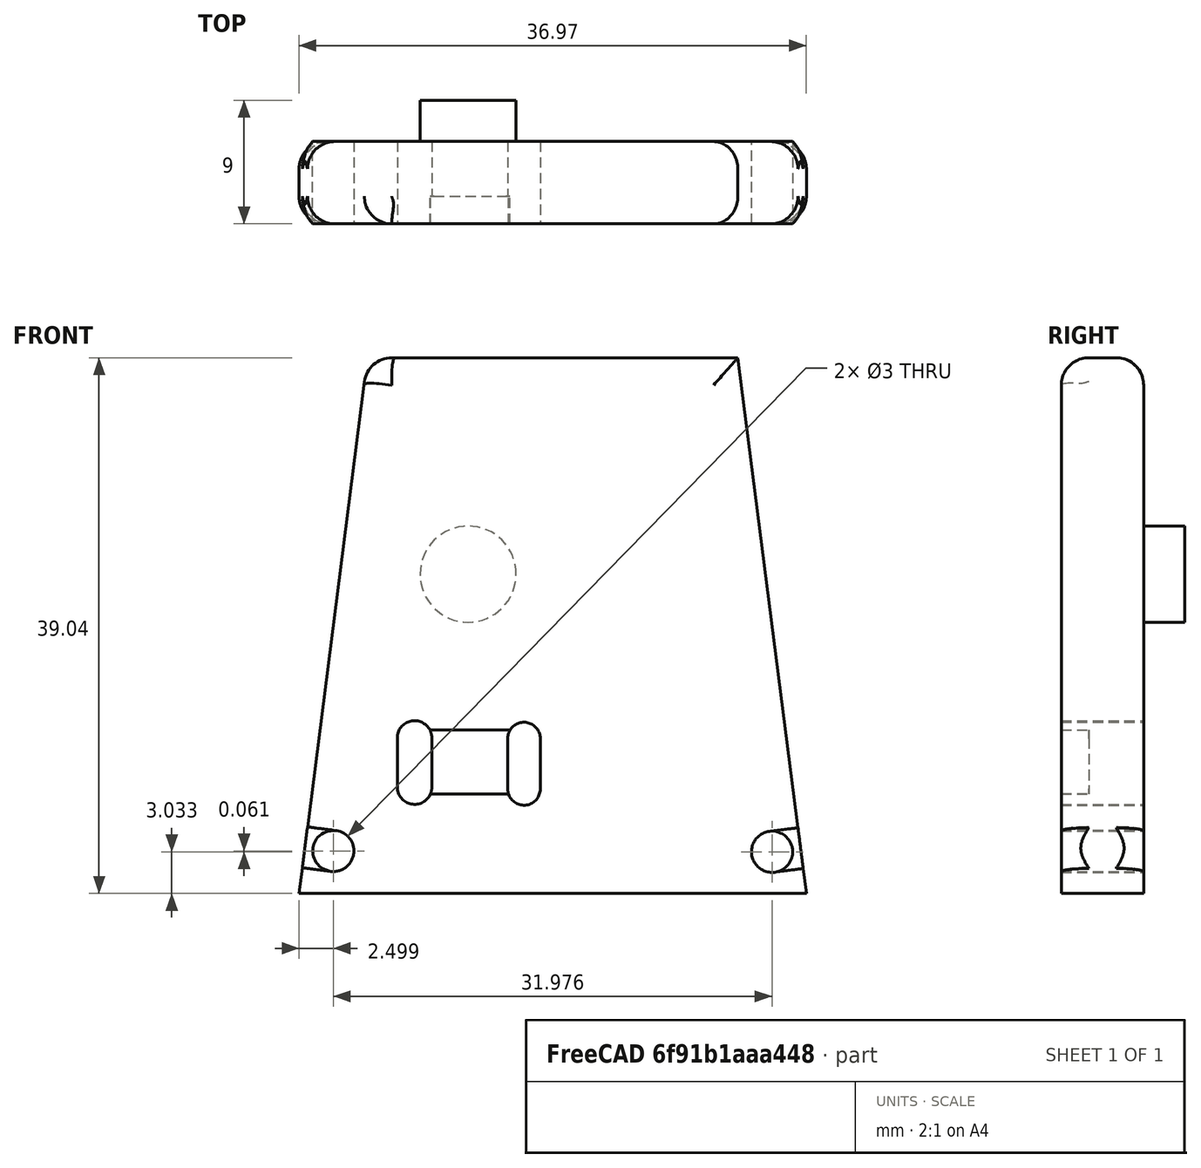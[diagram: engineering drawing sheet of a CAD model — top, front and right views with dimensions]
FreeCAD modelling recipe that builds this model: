
FCSTD DOCUMENT  (FreeCAD 0.17R13519 (Git))
Label: portaGPSinav2
License: All rights reserved
LicenseURL: http://it.wikipedia.org/wiki/<copyright redacted>
objects: Sketcher::SketchObject×5, PartDesign::Pocket×3, PartDesign::Fillet×3, PartDesign::Pad×2, Mesh::Feature×1, PartDesign::Body×1
note: 19 computed .brp shape members not serialized (recipe doc carries the construction recipe); baked Part::Feature solids carry a one-line shape summary decoded from their .brp

FEATURE [Mesh::Feature] ls210_sup
FEATURE [Sketcher::SketchObject] Sketch
  MapMode = 5
  Placement = pos=(0,0,0) rot=(1,0,0;1.5708rad)
  Support = -> [XZ_Plane]
  sketch-geometry (6):
    g0: LineSegment StartX=4.89923 StartY=141.911 StartZ=0 EndX=41.8748 EndY=141.911 EndZ=0
    g1: LineSegment StartX=41.8748 StartY=141.911 StartZ=0 EndX=36.8748 EndY=180.951 EndZ=0
    g2: LineSegment StartX=36.8748 StartY=180.951 StartZ=0 EndX=9.89923 EndY=180.951 EndZ=0
    g3: LineSegment StartX=9.89923 StartY=180.951 StartZ=0 EndX=4.89923 EndY=141.911 EndZ=0
    g4: GeomPoint X=7.39923 Y=144.73 Z=0
    g5: GeomPoint X=39.3748 Y=144.856 Z=0
  constraints (10):
    c: Coincident(g0,g1)
    c: Coincident(g1,g2)
    c: Coincident(g2,g3)
    c: Coincident(g3,g0)
    c: Horizontal(g0)
    c: Horizontal(g2)
    c: DistanceX(g0,g2) = 5
    c: DistanceX(g1,g0) = 5
    c: DistanceX(g0,g4) = 2.5
    c: DistanceX(g5,g0) = 2.5
FEATURE [PartDesign::Pad] Pad
  Length = 6
  Length2 = 100
  Placement = pos=(0,0,0) rot=(1,0,0;1.5708rad)
  Profile = -> Sketch
  Type = 0
FEATURE [Sketcher::SketchObject] Sketch001
  MapMode = 5
  Placement = pos=(0,0,0) rot=(-1,0,0;1.5708rad)
  Support = -> [Pad]
  sketch-geometry (1):
    g0: Circle CenterX=17.2244 CenterY=-165.178 CenterZ=0 NormalX=0 NormalY=0 NormalZ=1 AngleXU=0 Radius=3.5
  constraints (1):
    c: Radius(g0) = 3.5
FEATURE [PartDesign::Pad] Pad001
  BaseFeature = -> Pad
  Length = 3
  Length2 = 100
  Placement = pos=(0,0,0) rot=(1,0,0;1.5708rad)
  Profile = -> Sketch001
  Type = 0
FEATURE [Sketcher::SketchObject] Sketch002
  MapMode = 5
  Placement = pos=(0,0,0) rot=(-1,0,0;1.5708rad)
  Support = -> [Pad001]
  sketch-geometry (8):
    g0: ArcOfCircle CenterX=13.3212 CenterY=-153.239 CenterZ=0 NormalX=0 NormalY=0 NormalZ=1 AngleXU=0 Radius=1.2589 StartAngle=3.14159 EndAngle=6.28319
    g1: ArcOfCircle CenterX=13.3212 CenterY=-149.658 CenterZ=0 NormalX=0 NormalY=0 NormalZ=1 AngleXU=0 Radius=1.2589 StartAngle=0 EndAngle=3.14159
    g2: LineSegment StartX=14.5801 StartY=-153.239 StartZ=0 EndX=14.5801 EndY=-149.658 EndZ=0
    g3: LineSegment StartX=12.0623 StartY=-153.239 StartZ=0 EndX=12.0623 EndY=-149.658 EndZ=0
    g4: ArcOfCircle CenterX=21.2978 CenterY=-153.197 CenterZ=0 NormalX=0 NormalY=0 NormalZ=1 AngleXU=0 Radius=1.18673 StartAngle=3.14159 EndAngle=6.28319
    g5: ArcOfCircle CenterX=21.2978 CenterY=-149.524 CenterZ=0 NormalX=0 NormalY=0 NormalZ=1 AngleXU=0 Radius=1.18673 StartAngle=0 EndAngle=3.14159
    g6: LineSegment StartX=22.4845 StartY=-153.197 StartZ=0 EndX=22.4845 EndY=-149.524 EndZ=0
    g7: LineSegment StartX=20.1111 StartY=-153.197 StartZ=0 EndX=20.1111 EndY=-149.524 EndZ=0
  constraints (12):
    c: Tangent(g0,g3) = 1.5708
    c: Tangent(g0,g2) = -1.5708
    c: Tangent(g2,g1) = -1.5708
    c: Tangent(g3,g1) = 1.5708
    c: Vertical(g2)
    c: Equal(g0,g1)
    c: Tangent(g4,g7) = 1.5708
    c: Tangent(g4,g6) = -1.5708
    c: Tangent(g6,g5) = -1.5708
    c: Tangent(g7,g5) = 1.5708
    c: Vertical(g6)
    c: Equal(g4,g5)
FEATURE [PartDesign::Pocket] Pocket
  BaseFeature = -> Pad001
  Length = 6
  Length2 = 100
  Placement = pos=(0,0,0) rot=(1,0,0;1.5708rad)
  Profile = -> Sketch002
  Type = 0
FEATURE [Sketcher::SketchObject] Sketch003
  ExternalGeometry = -> [Pocket]
  MapMode = 5
  Placement = pos=(0,0,0) rot=(-1,0,0;1.5708rad)
  Support = -> [Pocket]
  sketch-geometry (2):
    g0: Circle CenterX=39.3748 CenterY=-144.943 CenterZ=0 NormalX=0 NormalY=0 NormalZ=1 AngleXU=0 Radius=1.5
    g1: Circle CenterX=7.39923 CenterY=-145.004 CenterZ=0 NormalX=0 NormalY=0 NormalZ=1 AngleXU=0 Radius=1.5
  constraints (4):
    c: Radius(g1) = 1.5
    c: Equal(g1,g0)
    c: DistanceX(g0,g-3) = 2.5
    c: DistanceX(g-3,g1) = 2.5
FEATURE [PartDesign::Pocket] Pocket001
  BaseFeature = -> Pocket
  Length = 6
  Length2 = 100
  Placement = pos=(0,0,0) rot=(1,0,0;1.5708rad)
  Profile = -> Sketch003
  Type = 0
FEATURE [Sketcher::SketchObject] Sketch004
  MapMode = 5
  Placement = pos=(0,-6,0) rot=(1,0,0;1.5708rad)
  Support = -> [Pocket]
  sketch-geometry (4):
    g0: ArcOfCircle CenterX=14.7376 CenterY=151.493 CenterZ=0 NormalX=0 NormalY=0 NormalZ=1 AngleXU=0 Radius=2.33606 StartAngle=1.5708 EndAngle=4.71239
    g1: ArcOfCircle CenterX=19.9684 CenterY=151.493 CenterZ=0 NormalX=0 NormalY=0 NormalZ=1 AngleXU=0 Radius=2.33606 StartAngle=4.71239 EndAngle=7.85398
    g2: LineSegment StartX=14.7376 StartY=149.157 StartZ=0 EndX=19.9684 EndY=149.157 EndZ=0
    g3: LineSegment StartX=14.7376 StartY=153.829 StartZ=0 EndX=19.9684 EndY=153.829 EndZ=0
  constraints (6):
    c: Tangent(g0,g3) = 1.5708
    c: Tangent(g0,g2) = -1.5708
    c: Tangent(g2,g1) = -1.5708
    c: Tangent(g3,g1) = 1.5708
    c: Horizontal(g2)
    c: Equal(g0,g1)
FEATURE [PartDesign::Pocket] Pocket002
  BaseFeature = -> Pocket001
  Length = 2
  Length2 = 100
  Placement = pos=(0,0,0) rot=(1,0,0;1.5708rad)
  Profile = -> Sketch004
  Type = 0
FEATURE [PartDesign::Fillet] Fillet
  Base = -> Pocket002 [Edge10,Edge23,Edge7]
  BaseFeature = -> Pocket002
  Placement = pos=(0,0,0) rot=(1,0,0;1.5708rad)
  Radius = 2
FEATURE [PartDesign::Fillet] Fillet001
  Base = -> Fillet [Edge7]
  BaseFeature = -> Fillet
  Placement = pos=(0,0,0) rot=(1,0,0;1.5708rad)
  Radius = 2
FEATURE [PartDesign::Fillet] Fillet002
  Base = -> Fillet001 [Edge17,Edge16,Edge4]
  BaseFeature = -> Fillet001
  Placement = pos=(0,0,0) rot=(1,0,0;1.5708rad)
  Radius = 2
FEATURE [PartDesign::Body] Body
  Group = -> [Sketch,Pad,Sketch001,Pad001,Sketch002,Pocket,Sketch003,Pocket001,Sketch004,Pocket002,Fillet,Fillet001,Fillet002]
  Origin = -> Origin
  Tip = -> Fillet002
